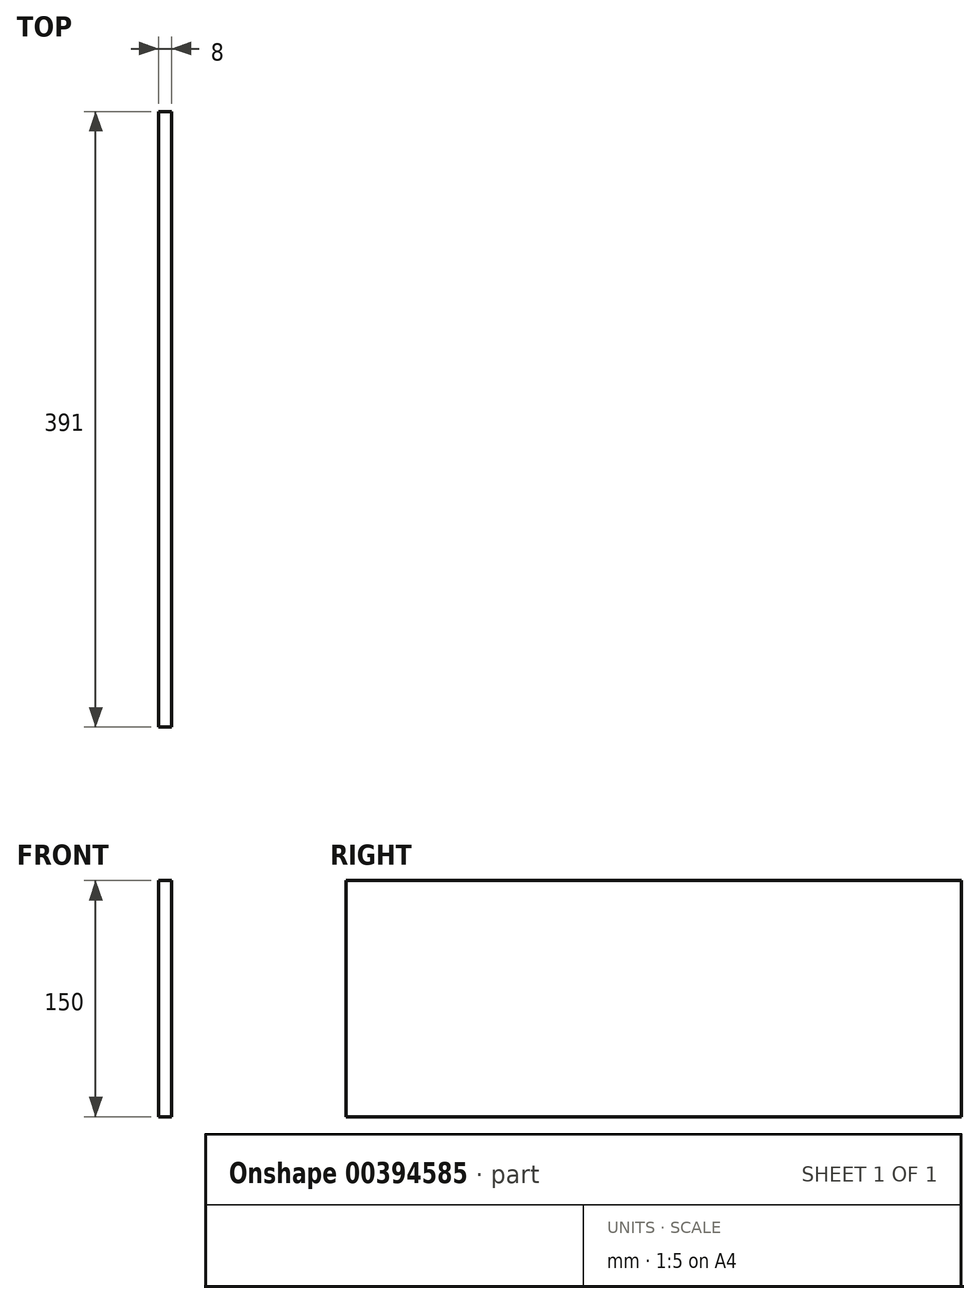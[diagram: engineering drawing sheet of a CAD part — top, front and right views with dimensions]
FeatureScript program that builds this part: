
annotation { "Feature Type Name" : "Feature", "Feature Type Description" : "" }
export const myFeature = defineFeature(function(context is Context, id is Id, definition is map)
    precondition{}
    {
        {
            var Q0;
            Q0=qCreatedBy(makeId("Right.planeOp"),FACE);
            var sketch = newSketch(context, id + "F0", { "sketchPlane" : qUnion([Q0])});
            skLineSegment(sketch, "E0.bottom", {"start": v(195.5, 75) * mm, "end": v(-195.5, 75) * mm});
            skLineSegment(sketch, "E0.top", {"start": v(195.5, -75) * mm, "end": v(-195.5, -75) * mm});
            skLineSegment(sketch, "E0.left", {"start": v(195.5, 75) * mm, "end": v(195.5, -75) * mm});
            skLineSegment(sketch, "E0.right", {"start": v(-195.5, 75) * mm, "end": v(-195.5, -75) * mm});
            skPoint(sketch, "E0.middle", {"position": v(0, 0) * mm});
            skSolve(sketch);
        }
        {
            var Q0;
            Q0=makeQuery(id+"F0.imprint","IMPRINT",FACE,{"disambiguationData":[TD([[makeQuery(id+"F0.imprint","IMPRINT",EDGE,{"derivedFrom":sQuery(id+"F0.wireOp",EDGE,"E0.bottom")}),1.0]])]});
            extrude(context, id + "F1", {"entities" : qUnion([Q0]), "depth" : 8 * mm});
        }
    });
